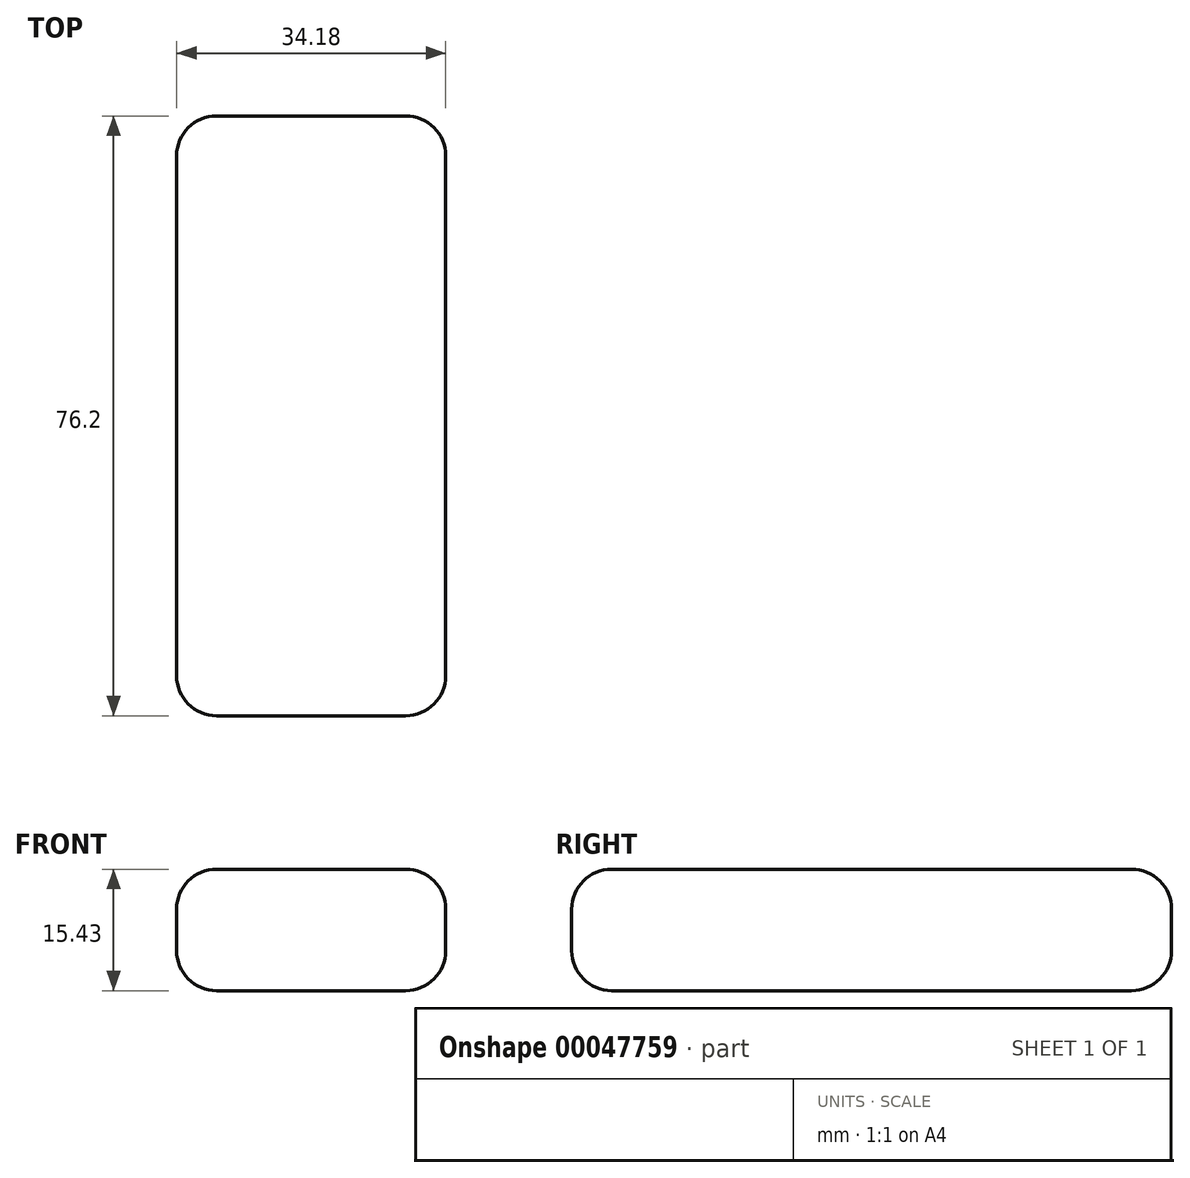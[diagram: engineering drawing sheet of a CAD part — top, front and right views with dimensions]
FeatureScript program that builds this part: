
annotation { "Feature Type Name" : "Feature", "Feature Type Description" : "" }
export const myFeature = defineFeature(function(context is Context, id is Id, definition is map)
    precondition{}
    {
        {
            var Q0;
            Q0=qCreatedBy(makeId("Front.planeOp"),FACE);
            var sketch = newSketch(context, id + "F0", { "sketchPlane" : qUnion([Q0])});
            skLineSegment(sketch, "E0.bottom", {"start": v(-59.9, 23.14) * mm, "end": v(-25.71, 23.14) * mm});
            skLineSegment(sketch, "E0.top", {"start": v(-59.9, 38.57) * mm, "end": v(-25.71, 38.57) * mm});
            skLineSegment(sketch, "E0.left", {"start": v(-59.9, 23.14) * mm, "end": v(-59.9, 38.57) * mm});
            skLineSegment(sketch, "E0.right", {"start": v(-25.71, 23.14) * mm, "end": v(-25.71, 38.57) * mm});
            skSolve(sketch);
        }
        {
            var Q0;
            Q0=makeQuery(id+"F0.imprint","IMPRINT",FACE,{"disambiguationData":[TD([[makeQuery(id+"F0.imprint","IMPRINT",EDGE,{"derivedFrom":sQuery(id+"F0.wireOp",EDGE,"E0.bottom")}),1.0]])]});
            var sketch = newSketch(context, id + "F1", { "sketchPlane" : qUnion([Q0])});
            skSolve(sketch);
        }
        {
            var Q0;
            Q0 = qSketchRegion(id + "F1", true);
            var Q1;
            Q1=makeQuery(id+"F0.imprint","IMPRINT",FACE,{"disambiguationData":[TD([[makeQuery(id+"F0.imprint","IMPRINT",EDGE,{"derivedFrom":sQuery(id+"F0.wireOp",EDGE,"E0.bottom")}),1.0]])]});
            extrude(context, id + "F2", {"entities" : qUnion([Q0, Q1]), "oppositeDirection" : true, "depth" : 76.2 * mm});
        }
        {
            var Q0;
            Q0=makeQuery(id+"F2.opExtrude","SWEPT_EDGE",EDGE,{"disambiguationData":[OSD([sQuery(id+"F0.wireOp",EDGE,"E0.top"),sQuery(id+"F0.wireOp",EDGE,"E0.left")])]});
            var Q1;
            Q1=makeQuery(id+"F2.opExtrude","CAP_EDGE",EDGE,{"disambiguationData":[OSD([sQuery(id+"F0.wireOp",EDGE,"E0.top")])],"isStart":false});
            var Q2;
            Q2=makeQuery(id+"F2.opExtrude","CAP_EDGE",EDGE,{"disambiguationData":[OSD([sQuery(id+"F0.wireOp",EDGE,"E0.bottom")])],"isStart":false});
            var Q3;
            Q3=makeQuery(id+"F2.opExtrude","SWEPT_EDGE",EDGE,{"disambiguationData":[OSD([sQuery(id+"F0.wireOp",EDGE,"E0.bottom"),sQuery(id+"F0.wireOp",EDGE,"E0.left")])]});
            var Q4;
            Q4=makeQuery(id+"F2.opExtrude","CAP_EDGE",EDGE,{"disambiguationData":[OSD([sQuery(id+"F0.wireOp",EDGE,"E0.left")])],"isStart":true});
            var Q5;
            Q5=makeQuery(id+"F2.opExtrude","CAP_EDGE",EDGE,{"disambiguationData":[OSD([sQuery(id+"F0.wireOp",EDGE,"E0.left")])],"isStart":false});
            var Q6;
            Q6=makeQuery(id+"F2.opExtrude","CAP_EDGE",EDGE,{"disambiguationData":[OSD([sQuery(id+"F0.wireOp",EDGE,"E0.right")])],"isStart":false});
            var Q7;
            Q7=makeQuery(id+"F2.opExtrude","SWEPT_EDGE",EDGE,{"disambiguationData":[OSD([sQuery(id+"F0.wireOp",EDGE,"E0.top"),sQuery(id+"F0.wireOp",EDGE,"E0.right")])]});
            var Q8;
            Q8=makeQuery(id+"F2.opExtrude","CAP_EDGE",EDGE,{"disambiguationData":[OSD([sQuery(id+"F0.wireOp",EDGE,"E0.top")])],"isStart":true});
            var Q9;
            Q9=makeQuery(id+"F2.opExtrude","CAP_EDGE",EDGE,{"disambiguationData":[OSD([sQuery(id+"F0.wireOp",EDGE,"E0.bottom")])],"isStart":true});
            var Q10;
            Q10=makeQuery(id+"F2.opExtrude","SWEPT_EDGE",EDGE,{"disambiguationData":[OSD([sQuery(id+"F0.wireOp",EDGE,"E0.bottom"),sQuery(id+"F0.wireOp",EDGE,"E0.right")])]});
            var Q11;
            Q11=makeQuery(id+"F2.opExtrude","CAP_EDGE",EDGE,{"disambiguationData":[OSD([sQuery(id+"F0.wireOp",EDGE,"E0.right")])],"isStart":true});
            fillet(context, id + "F3", {"entities" : qUnion([Q0, Q1, Q2, Q3, Q4, Q5, Q6, Q7, Q8, Q9, Q10, Q11]), "radius" : 5.08 * mm, "tangentPropagation" : true, "allowEdgeOverflow" : false});
        }
    });
